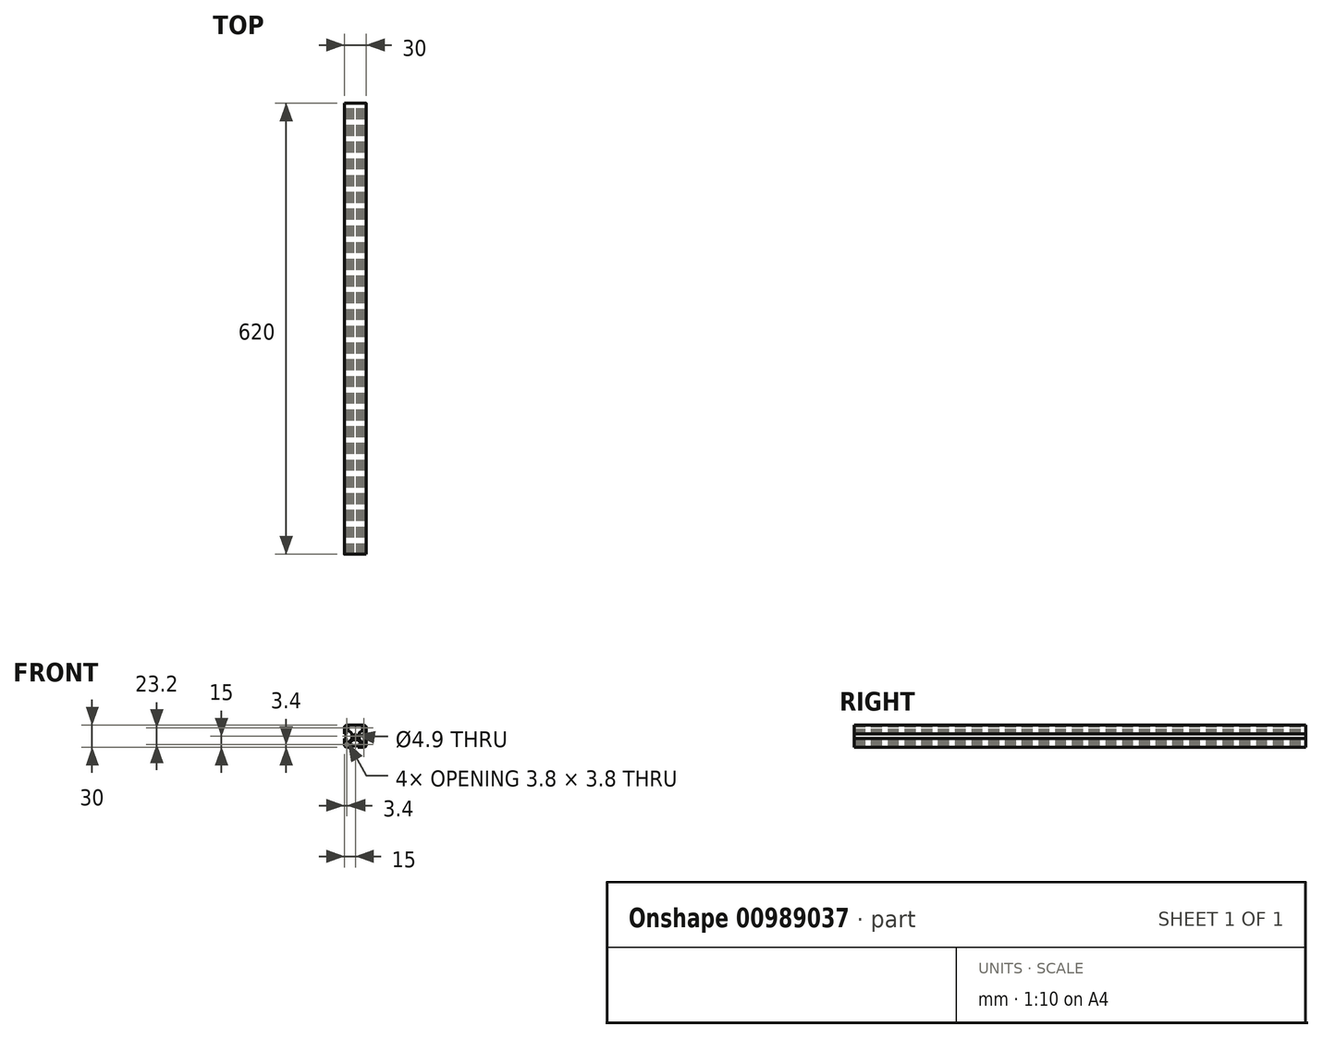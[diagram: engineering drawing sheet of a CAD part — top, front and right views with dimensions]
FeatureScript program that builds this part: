
annotation { "Feature Type Name" : "Feature", "Feature Type Description" : "" }
export const myFeature = defineFeature(function(context is Context, id is Id, definition is map)
    precondition{}
    {
        {
            var Q0;
            Q0=qCreatedBy(makeId("Front.planeOp"),FACE);
            var sketch = newSketch(context, id + "F0", { "sketchPlane" : qUnion([Q0])});
            skLineSegment(sketch, "E0.bottom", {"start": v(-12, 15) * mm, "end": v(12, 15) * mm});
            skLineSegment(sketch, "E0.top", {"start": v(-12, -15) * mm, "end": v(12, -15) * mm});
            skLineSegment(sketch, "E0.left", {"start": v(-15, 12) * mm, "end": v(-15, -12) * mm});
            skLineSegment(sketch, "E0.right", {"start": v(15, 12) * mm, "end": v(15, -12) * mm});
            skPoint(sketch, "E1.visualSharp", {"position": v(-15, 15) * mm});
            skArc(sketch, "E1.filletArc", {"start": v(-12, 15) * mm, "mid": v(-14.12, 14.12) * mm, "end": v(-15, 12) * mm});
            skPoint(sketch, "E2.visualSharp", {"position": v(15, 15) * mm});
            skArc(sketch, "E2.filletArc", {"start": v(15, 12) * mm, "mid": v(14.12, 14.12) * mm, "end": v(12, 15) * mm});
            skPoint(sketch, "E3.visualSharp", {"position": v(15, -15) * mm});
            skArc(sketch, "E3.filletArc", {"start": v(12, -15) * mm, "mid": v(14.12, -14.12) * mm, "end": v(15, -12) * mm});
            skPoint(sketch, "E4.visualSharp", {"position": v(-15, -15) * mm});
            skArc(sketch, "E4.filletArc", {"start": v(-15, -12) * mm, "mid": v(-14.12, -14.12) * mm, "end": v(-12, -15) * mm});
            skCircle(sketch, "E5", {"center": v(0, 0) * mm, "radius": 2.45 * mm});
            skPoint(sketch, "E6", {"position": v(15, 8.22) * mm});
            skPoint(sketch, "E7", {"position": v(15, -8.22) * mm});
            skPoint(sketch, "E8", {"position": v(15, 3.17) * mm});
            skPoint(sketch, "E9", {"position": v(15, -3.18) * mm});
            skLineSegment(sketch, "E10", {"start": v(15, 3.17) * mm, "end": v(13.09, 3.17) * mm});
            skLineSegment(sketch, "E11", {"start": v(13.09, -3.18) * mm, "end": v(15, -3.18) * mm});
            skPoint(sketch, "E12", {"position": v(12.06, -5.83) * mm});
            skPoint(sketch, "E13", {"position": v(12.06, 5.82) * mm});
            skPoint(sketch, "E14", {"position": v(13.5, -5.82) * mm});
            skPoint(sketch, "E15", {"position": v(13.5, 5.82) * mm});
            skPoint(sketch, "E16", {"position": v(13.5, 8.22) * mm});
            skPoint(sketch, "E17", {"position": v(13.5, -8.22) * mm});
            skPoint(sketch, "E18", {"position": v(9.5, 8.22) * mm});
            skPoint(sketch, "E19", {"position": v(9.5, -8.22) * mm});
            skPoint(sketch, "E20", {"position": v(5.1, -3.92) * mm});
            skPoint(sketch, "E21", {"position": v(5.1, 4.08) * mm});
            skLineSegment(sketch, "E22", {"start": v(12.09, -4.16) * mm, "end": v(12.08, -4.81) * mm});
            skLineSegment(sketch, "E23", {"start": v(13.5, -5.82) * mm, "end": v(13.5, -8.22) * mm});
            skLineSegment(sketch, "E24", {"start": v(9.2, -7.94) * mm, "end": v(5.4, -4.21) * mm});
            skLineSegment(sketch, "E25", {"start": v(5.1, 3.65) * mm, "end": v(5.1, -3.5) * mm});
            skLineSegment(sketch, "E26", {"start": v(5.41, 4.38) * mm, "end": v(9.21, 7.95) * mm});
            skLineSegment(sketch, "E27", {"start": v(13.5, 8.22) * mm, "end": v(9.9, 8.22) * mm});
            skLineSegment(sketch, "E28", {"start": v(13.5, 8.22) * mm, "end": v(13.5, 5.82) * mm});
            skLineSegment(sketch, "E29", {"start": v(13.08, 5.82) * mm, "end": v(13.5, 5.82) * mm});
            skLineSegment(sketch, "E30", {"start": v(12.08, 4.81) * mm, "end": v(12.09, 4.16) * mm});
            skLineSegment(sketch, "E31", {"start": v(13.08, -5.83) * mm, "end": v(13.5, -5.83) * mm});
            skLineSegment(sketch, "E32", {"start": v(13.5, -8.22) * mm, "end": v(9.9, -8.22) * mm});
            skLineSegment(sketch, "E33", {"start": v(13.5, -8.22) * mm, "end": v(13.5, -5.82) * mm});
            skArc(sketch, "E34.filletArc", {"start": v(9.9, 8.22) * mm, "mid": v(9.53, 8.15) * mm, "end": v(9.21, 7.95) * mm});
            skArc(sketch, "E35.filletArc", {"start": v(5.41, 4.38) * mm, "mid": v(5.18, 4.04) * mm, "end": v(5.1, 3.65) * mm});
            skArc(sketch, "E36.filletArc", {"start": v(5.1, -3.5) * mm, "mid": v(5.18, -3.89) * mm, "end": v(5.4, -4.21) * mm});
            skArc(sketch, "E37.filletArc", {"start": v(9.2, -7.94) * mm, "mid": v(9.53, -8.15) * mm, "end": v(9.9, -8.22) * mm});
            skArc(sketch, "E38.filletArc", {"start": v(12.08, -4.81) * mm, "mid": v(12.36, -5.53) * mm, "end": v(13.08, -5.83) * mm});
            skPoint(sketch, "E39.visualSharp", {"position": v(12.1, -3.18) * mm});
            skArc(sketch, "E39.filletArc", {"start": v(13.09, -3.18) * mm, "mid": v(12.38, -3.46) * mm, "end": v(12.09, -4.16) * mm});
            skPoint(sketch, "E40.visualSharp", {"position": v(12.1, 3.17) * mm});
            skArc(sketch, "E40.filletArc", {"start": v(12.09, 4.16) * mm, "mid": v(12.38, 3.46) * mm, "end": v(13.09, 3.17) * mm});
            skArc(sketch, "E41.filletArc", {"start": v(13.08, 5.82) * mm, "mid": v(12.36, 5.53) * mm, "end": v(12.08, 4.81) * mm});
            skArc(sketch, "E42.MirrorCS", {"start": v(-5.1, -3.5) * mm, "mid": v(-5.18, -3.89) * mm, "end": v(-5.4, -4.21) * mm});
            skLineSegment(sketch, "E43.MirrorCS", {"start": v(-13.08, -5.83) * mm, "end": v(-13.5, -5.83) * mm});
            skArc(sketch, "E44.MirrorCS", {"start": v(-9.2, -7.94) * mm, "mid": v(-9.53, -8.15) * mm, "end": v(-9.9, -8.22) * mm});
            skLineSegment(sketch, "E45.MirrorCS", {"start": v(-13.08, 5.82) * mm, "end": v(-13.5, 5.82) * mm});
            skArc(sketch, "E46.MirrorCS", {"start": v(-5.41, 4.38) * mm, "mid": v(-5.18, 4.04) * mm, "end": v(-5.1, 3.65) * mm});
            skArc(sketch, "E47.MirrorCS", {"start": v(-9.9, 8.22) * mm, "mid": v(-9.53, 8.15) * mm, "end": v(-9.21, 7.95) * mm});
            skArc(sketch, "E48.MirrorCS", {"start": v(-13.08, 5.82) * mm, "mid": v(-12.36, 5.53) * mm, "end": v(-12.08, 4.81) * mm});
            skLineSegment(sketch, "E49.MirrorCS", {"start": v(-12.08, 4.81) * mm, "end": v(-12.09, 4.16) * mm});
            skLineSegment(sketch, "E50.MirrorCS", {"start": v(-12.09, -4.16) * mm, "end": v(-12.08, -4.81) * mm});
            skArc(sketch, "E51.MirrorCS", {"start": v(-12.08, -4.81) * mm, "mid": v(-12.36, -5.53) * mm, "end": v(-13.08, -5.83) * mm});
            skLineSegment(sketch, "E52.MirrorCS", {"start": v(-13.5, -8.22) * mm, "end": v(-13.5, -5.82) * mm});
            skLineSegment(sketch, "E53.MirrorCS", {"start": v(-13.5, -5.82) * mm, "end": v(-13.5, -8.22) * mm});
            skLineSegment(sketch, "E54.MirrorCS", {"start": v(-13.09, -3.18) * mm, "end": v(-15, -3.18) * mm});
            skArc(sketch, "E55.MirrorCS", {"start": v(-12.09, 4.16) * mm, "mid": v(-12.38, 3.46) * mm, "end": v(-13.09, 3.17) * mm});
            skArc(sketch, "E56.MirrorCS", {"start": v(-13.09, -3.18) * mm, "mid": v(-12.38, -3.46) * mm, "end": v(-12.09, -4.16) * mm});
            skLineSegment(sketch, "E57.MirrorCS", {"start": v(-15, 3.17) * mm, "end": v(-13.09, 3.17) * mm});
            skPoint(sketch, "E58.MirrorP", {"position": v(-5.1, -3.92) * mm});
            skPoint(sketch, "E59.MirrorP", {"position": v(-9.5, -8.22) * mm});
            skPoint(sketch, "E60.MirrorP", {"position": v(-13.5, -8.22) * mm});
            skPoint(sketch, "E61.MirrorP", {"position": v(-12.06, 5.82) * mm});
            skPoint(sketch, "E62.MirrorP", {"position": v(-5.1, 4.08) * mm});
            skLineSegment(sketch, "E63.MirrorCS", {"start": v(-13.5, 8.22) * mm, "end": v(-13.5, 5.82) * mm});
            skPoint(sketch, "E64.MirrorP", {"position": v(-12.06, -5.83) * mm});
            skPoint(sketch, "E65.MirrorP", {"position": v(-9.5, 8.22) * mm});
            skPoint(sketch, "E66.MirrorP", {"position": v(-15, 8.22) * mm});
            skPoint(sketch, "E67.MirrorP", {"position": v(-13.5, 5.82) * mm});
            skLineSegment(sketch, "E68.MirrorCS", {"start": v(-13.5, 8.22) * mm, "end": v(-9.9, 8.22) * mm});
            skPoint(sketch, "E69.MirrorP", {"position": v(-13.5, -5.82) * mm});
            skLineSegment(sketch, "E70.MirrorCS", {"start": v(-13.5, -8.22) * mm, "end": v(-9.9, -8.22) * mm});
            skLineSegment(sketch, "E71.MirrorCS", {"start": v(-5.1, 3.65) * mm, "end": v(-5.1, -3.5) * mm});
            skPoint(sketch, "E72.MirrorP", {"position": v(-13.5, 8.22) * mm});
            skPoint(sketch, "E73.MirrorP", {"position": v(-15, -3.18) * mm});
            skPoint(sketch, "E74.MirrorP", {"position": v(-12.1, 3.17) * mm});
            skPoint(sketch, "E75.MirrorP", {"position": v(-15, -8.22) * mm});
            skPoint(sketch, "E76.MirrorP", {"position": v(-12.1, -3.18) * mm});
            skLineSegment(sketch, "E77.MirrorCS", {"start": v(-5.41, 4.38) * mm, "end": v(-9.21, 7.95) * mm});
            skLineSegment(sketch, "E78.MirrorCS", {"start": v(-9.2, -7.94) * mm, "end": v(-5.4, -4.21) * mm});
            skPoint(sketch, "E79.MirrorP", {"position": v(-15, 3.17) * mm});
            skArc(sketch, "E80.MirrorCS", {"start": v(-3.5, 5.1) * mm, "mid": v(-3.89, 5.18) * mm, "end": v(-4.21, 5.4) * mm});
            skLineSegment(sketch, "E81.MirrorCS", {"start": v(-5.82, 13.08) * mm, "end": v(-5.82, 13.5) * mm});
            skArc(sketch, "E82.MirrorCS", {"start": v(-7.94, 9.2) * mm, "mid": v(-8.15, 9.53) * mm, "end": v(-8.22, 9.9) * mm});
            skLineSegment(sketch, "E83.MirrorCS", {"start": v(5.83, 13.08) * mm, "end": v(5.83, 13.5) * mm});
            skArc(sketch, "E84.MirrorCS", {"start": v(4.38, 5.41) * mm, "mid": v(4.04, 5.18) * mm, "end": v(3.65, 5.1) * mm});
            skArc(sketch, "E85.MirrorCS", {"start": v(8.23, 9.9) * mm, "mid": v(8.15, 9.53) * mm, "end": v(7.95, 9.21) * mm});
            skArc(sketch, "E86.MirrorCS", {"start": v(5.83, 13.08) * mm, "mid": v(5.53, 12.36) * mm, "end": v(4.81, 12.08) * mm});
            skLineSegment(sketch, "E87.MirrorCS", {"start": v(4.81, 12.08) * mm, "end": v(4.16, 12.09) * mm});
            skLineSegment(sketch, "E88.MirrorCS", {"start": v(-4.16, 12.09) * mm, "end": v(-4.81, 12.08) * mm});
            skArc(sketch, "E89.MirrorCS", {"start": v(-4.81, 12.08) * mm, "mid": v(-5.53, 12.36) * mm, "end": v(-5.82, 13.08) * mm});
            skLineSegment(sketch, "E90.MirrorCS", {"start": v(-8.22, 13.5) * mm, "end": v(-5.82, 13.5) * mm});
            skLineSegment(sketch, "E91.MirrorCS", {"start": v(-5.82, 13.5) * mm, "end": v(-8.22, 13.5) * mm});
            skLineSegment(sketch, "E92.MirrorCS", {"start": v(-3.17, 13.09) * mm, "end": v(-3.17, 15) * mm});
            skArc(sketch, "E93.MirrorCS", {"start": v(4.16, 12.09) * mm, "mid": v(3.46, 12.38) * mm, "end": v(3.18, 13.09) * mm});
            skArc(sketch, "E94.MirrorCS", {"start": v(-3.17, 13.09) * mm, "mid": v(-3.46, 12.38) * mm, "end": v(-4.16, 12.09) * mm});
            skLineSegment(sketch, "E95.MirrorCS", {"start": v(3.18, 15) * mm, "end": v(3.18, 13.09) * mm});
            skPoint(sketch, "E96.MirrorP", {"position": v(-3.92, 5.1) * mm});
            skPoint(sketch, "E97.MirrorP", {"position": v(-8.22, 9.5) * mm});
            skPoint(sketch, "E98.MirrorP", {"position": v(-8.22, 13.5) * mm});
            skPoint(sketch, "E99.MirrorP", {"position": v(5.83, 12.06) * mm});
            skPoint(sketch, "E100.MirrorP", {"position": v(4.08, 5.1) * mm});
            skLineSegment(sketch, "E101.MirrorCS", {"start": v(8.23, 13.5) * mm, "end": v(5.83, 13.5) * mm});
            skPoint(sketch, "E102.MirrorP", {"position": v(-5.82, 12.06) * mm});
            skPoint(sketch, "E103.MirrorP", {"position": v(8.23, 9.5) * mm});
            skPoint(sketch, "E104.MirrorP", {"position": v(8.23, 15) * mm});
            skPoint(sketch, "E105.MirrorP", {"position": v(5.83, 13.5) * mm});
            skLineSegment(sketch, "E106.MirrorCS", {"start": v(8.23, 13.5) * mm, "end": v(8.23, 9.9) * mm});
            skPoint(sketch, "E107.MirrorP", {"position": v(-5.82, 13.5) * mm});
            skLineSegment(sketch, "E108.MirrorCS", {"start": v(-8.22, 13.5) * mm, "end": v(-8.22, 9.9) * mm});
            skLineSegment(sketch, "E109.MirrorCS", {"start": v(3.65, 5.1) * mm, "end": v(-3.5, 5.1) * mm});
            skPoint(sketch, "E110.MirrorP", {"position": v(8.23, 13.5) * mm});
            skPoint(sketch, "E111.MirrorP", {"position": v(-3.17, 15) * mm});
            skPoint(sketch, "E112.MirrorP", {"position": v(3.18, 12.1) * mm});
            skPoint(sketch, "E113.MirrorP", {"position": v(-8.22, 15) * mm});
            skPoint(sketch, "E114.MirrorP", {"position": v(-3.17, 12.1) * mm});
            skLineSegment(sketch, "E115.MirrorCS", {"start": v(4.38, 5.41) * mm, "end": v(7.95, 9.21) * mm});
            skLineSegment(sketch, "E116.MirrorCS", {"start": v(-7.94, 9.2) * mm, "end": v(-4.21, 5.4) * mm});
            skPoint(sketch, "E117.MirrorP", {"position": v(3.18, 15) * mm});
            skPoint(sketch, "E118", {"position": v(-8.22, -15) * mm});
            skArc(sketch, "E119.MirrorCS", {"start": v(3.5, -5.1) * mm, "mid": v(3.89, -5.18) * mm, "end": v(4.21, -5.4) * mm});
            skLineSegment(sketch, "E120.MirrorCS", {"start": v(5.83, -13.08) * mm, "end": v(5.83, -13.5) * mm});
            skArc(sketch, "E121.MirrorCS", {"start": v(7.94, -9.2) * mm, "mid": v(8.15, -9.53) * mm, "end": v(8.23, -9.9) * mm});
            skLineSegment(sketch, "E122.MirrorCS", {"start": v(-5.82, -13.08) * mm, "end": v(-5.82, -13.5) * mm});
            skArc(sketch, "E123.MirrorCS", {"start": v(-4.38, -5.41) * mm, "mid": v(-4.04, -5.18) * mm, "end": v(-3.65, -5.1) * mm});
            skArc(sketch, "E124.MirrorCS", {"start": v(-8.22, -9.9) * mm, "mid": v(-8.15, -9.53) * mm, "end": v(-7.95, -9.21) * mm});
            skArc(sketch, "E125.MirrorCS", {"start": v(-5.82, -13.08) * mm, "mid": v(-5.53, -12.36) * mm, "end": v(-4.81, -12.08) * mm});
            skLineSegment(sketch, "E126.MirrorCS", {"start": v(-4.81, -12.08) * mm, "end": v(-4.16, -12.09) * mm});
            skLineSegment(sketch, "E127.MirrorCS", {"start": v(4.16, -12.09) * mm, "end": v(4.81, -12.08) * mm});
            skArc(sketch, "E128.MirrorCS", {"start": v(4.81, -12.08) * mm, "mid": v(5.53, -12.36) * mm, "end": v(5.83, -13.08) * mm});
            skLineSegment(sketch, "E129.MirrorCS", {"start": v(8.23, -13.5) * mm, "end": v(5.83, -13.5) * mm});
            skLineSegment(sketch, "E130.MirrorCS", {"start": v(5.83, -13.5) * mm, "end": v(8.23, -13.5) * mm});
            skLineSegment(sketch, "E131.MirrorCS", {"start": v(3.18, -13.09) * mm, "end": v(3.18, -15) * mm});
            skArc(sketch, "E132.MirrorCS", {"start": v(-4.16, -12.09) * mm, "mid": v(-3.46, -12.38) * mm, "end": v(-3.17, -13.09) * mm});
            skArc(sketch, "E133.MirrorCS", {"start": v(3.18, -13.09) * mm, "mid": v(3.46, -12.38) * mm, "end": v(4.16, -12.09) * mm});
            skLineSegment(sketch, "E134.MirrorCS", {"start": v(-3.17, -15) * mm, "end": v(-3.17, -13.09) * mm});
            skPoint(sketch, "E135.MirrorP", {"position": v(3.92, -5.1) * mm});
            skPoint(sketch, "E136.MirrorP", {"position": v(8.23, -9.5) * mm});
            skPoint(sketch, "E137.MirrorP", {"position": v(8.23, -13.5) * mm});
            skPoint(sketch, "E138.MirrorP", {"position": v(-5.82, -12.06) * mm});
            skPoint(sketch, "E139.MirrorP", {"position": v(-4.08, -5.1) * mm});
            skLineSegment(sketch, "E140.MirrorCS", {"start": v(-8.22, -13.5) * mm, "end": v(-5.82, -13.5) * mm});
            skPoint(sketch, "E141.MirrorP", {"position": v(5.83, -12.06) * mm});
            skPoint(sketch, "E142.MirrorP", {"position": v(-8.22, -9.5) * mm});
            skPoint(sketch, "E143.MirrorP", {"position": v(-5.82, -13.5) * mm});
            skLineSegment(sketch, "E144.MirrorCS", {"start": v(-8.22, -13.5) * mm, "end": v(-8.22, -9.9) * mm});
            skPoint(sketch, "E145.MirrorP", {"position": v(5.83, -13.5) * mm});
            skLineSegment(sketch, "E146.MirrorCS", {"start": v(8.23, -13.5) * mm, "end": v(8.23, -9.9) * mm});
            skLineSegment(sketch, "E147.MirrorCS", {"start": v(-3.65, -5.1) * mm, "end": v(3.5, -5.1) * mm});
            skPoint(sketch, "E148.MirrorP", {"position": v(-8.22, -13.5) * mm});
            skPoint(sketch, "E149.MirrorP", {"position": v(3.18, -15) * mm});
            skPoint(sketch, "E150.MirrorP", {"position": v(-3.17, -12.1) * mm});
            skPoint(sketch, "E151.MirrorP", {"position": v(8.23, -15) * mm});
            skPoint(sketch, "E152.MirrorP", {"position": v(3.18, -12.1) * mm});
            skLineSegment(sketch, "E153.MirrorCS", {"start": v(-4.38, -5.41) * mm, "end": v(-7.95, -9.21) * mm});
            skLineSegment(sketch, "E154.MirrorCS", {"start": v(7.94, -9.2) * mm, "end": v(4.21, -5.4) * mm});
            skPoint(sketch, "E155.MirrorP", {"position": v(-3.17, -15) * mm});
            skLineSegment(sketch, "E156.bottom", {"start": v(-13.5, -9.7) * mm, "end": v(-9.7, -9.7) * mm});
            skLineSegment(sketch, "E156.top", {"start": v(-11.5, -13.5) * mm, "end": v(-9.7, -13.5) * mm});
            skLineSegment(sketch, "E156.left", {"start": v(-13.5, -9.7) * mm, "end": v(-13.5, -11.5) * mm});
            skLineSegment(sketch, "E156.right", {"start": v(-9.7, -9.7) * mm, "end": v(-9.7, -13.5) * mm});
            skPoint(sketch, "E157.visualSharp", {"position": v(-13.5, -13.5) * mm});
            skArc(sketch, "E157.filletArc", {"start": v(-13.5, -11.5) * mm, "mid": v(-12.91, -12.91) * mm, "end": v(-11.5, -13.5) * mm});
            skPoint(sketch, "E158", {"position": v(-11.6, -11.6) * mm});
            skPoint(sketch, "E159.MirrorP", {"position": v(-11.6, 11.6) * mm});
            skLineSegment(sketch, "E160.MirrorCS", {"start": v(-11.5, 13.5) * mm, "end": v(-9.7, 13.5) * mm});
            skLineSegment(sketch, "E161.MirrorCS", {"start": v(-9.7, 9.7) * mm, "end": v(-9.7, 13.5) * mm});
            skLineSegment(sketch, "E162.MirrorCS", {"start": v(-13.5, 9.7) * mm, "end": v(-9.7, 9.7) * mm});
            skLineSegment(sketch, "E163.MirrorCS", {"start": v(-13.5, 9.7) * mm, "end": v(-13.5, 11.5) * mm});
            skPoint(sketch, "E164.MirrorP", {"position": v(-13.5, 13.5) * mm});
            skArc(sketch, "E165.MirrorCS", {"start": v(-13.5, 11.5) * mm, "mid": v(-12.91, 12.91) * mm, "end": v(-11.5, 13.5) * mm});
            skPoint(sketch, "E166.MirrorP", {"position": v(11.6, 11.6) * mm});
            skLineSegment(sketch, "E167.MirrorCS", {"start": v(11.5, 13.5) * mm, "end": v(9.7, 13.5) * mm});
            skLineSegment(sketch, "E168.MirrorCS", {"start": v(13.5, 9.7) * mm, "end": v(9.7, 9.7) * mm});
            skLineSegment(sketch, "E169.MirrorCS", {"start": v(9.7, 9.7) * mm, "end": v(9.7, 13.5) * mm});
            skLineSegment(sketch, "E170.MirrorCS", {"start": v(13.5, 9.7) * mm, "end": v(13.5, 11.5) * mm});
            skArc(sketch, "E171.MirrorCS", {"start": v(13.5, 11.5) * mm, "mid": v(12.91, 12.91) * mm, "end": v(11.5, 13.5) * mm});
            skPoint(sketch, "E172.MirrorP", {"position": v(11.6, -11.6) * mm});
            skLineSegment(sketch, "E173.MirrorCS", {"start": v(13.5, -9.7) * mm, "end": v(13.5, -11.5) * mm});
            skArc(sketch, "E174.MirrorCS", {"start": v(13.5, -11.5) * mm, "mid": v(12.91, -12.91) * mm, "end": v(11.5, -13.5) * mm});
            skLineSegment(sketch, "E175.MirrorCS", {"start": v(13.5, -9.7) * mm, "end": v(9.7, -9.7) * mm});
            skLineSegment(sketch, "E176.MirrorCS", {"start": v(9.7, -9.7) * mm, "end": v(9.7, -13.5) * mm});
            skLineSegment(sketch, "E177.MirrorCS", {"start": v(11.5, -13.5) * mm, "end": v(9.7, -13.5) * mm});
            skSolve(sketch);
        }
        {
            var Q0;
            {var subQ13=sQuery(id+"F0.wireOp",EDGE,"E1.filletArc");Q0=makeQuery(id+"F0.imprint","IMPRINT",FACE,{"disambiguationData":[TD([[makeQuery(id+"F0.imprint","IMPRINT",EDGE,{"derivedFrom":subQ13}),1.0]])]});}
            extrude(context, id + "F1", {"entities" : qUnion([Q0]), "depth" : 460 * mm, "offsetDistance" : 25 * mm});
        }
        {
            var Q0;
            Q0=makeQuery(id+"F1.opExtrude","CAP_FACE",FACE,{"disambiguationData":[OSD([sQuery(id+"F0.wireOp",EDGE,"E0.bottom"),sQuery(id+"F0.wireOp",EDGE,"E0.top"),sQuery(id+"F0.wireOp",EDGE,"E0.left"),sQuery(id+"F0.wireOp",EDGE,"E0.right"),sQuery(id+"F0.wireOp",EDGE,"E1.filletArc"),sQuery(id+"F0.wireOp",EDGE,"E2.filletArc"),sQuery(id+"F0.wireOp",EDGE,"E3.filletArc"),sQuery(id+"F0.wireOp",EDGE,"E4.filletArc"),sQuery(id+"F0.wireOp",EDGE,"E5"),sQuery(id+"F0.wireOp",EDGE,"E10"),sQuery(id+"F0.wireOp",EDGE,"E11"),sQuery(id+"F0.wireOp",EDGE,"E22"),sQuery(id+"F0.wireOp",EDGE,"E24"),sQuery(id+"F0.wireOp",EDGE,"E25"),sQuery(id+"F0.wireOp",EDGE,"E26"),sQuery(id+"F0.wireOp",EDGE,"E27"),sQuery(id+"F0.wireOp",EDGE,"E28"),sQuery(id+"F0.wireOp",EDGE,"E29"),sQuery(id+"F0.wireOp",EDGE,"E30"),sQuery(id+"F0.wireOp",EDGE,"E31"),sQuery(id+"F0.wireOp",EDGE,"E32"),sQuery(id+"F0.wireOp",EDGE,"E33"),sQuery(id+"F0.wireOp",EDGE,"E34.filletArc"),sQuery(id+"F0.wireOp",EDGE,"E35.filletArc"),sQuery(id+"F0.wireOp",EDGE,"E36.filletArc"),sQuery(id+"F0.wireOp",EDGE,"E37.filletArc"),sQuery(id+"F0.wireOp",EDGE,"E38.filletArc"),sQuery(id+"F0.wireOp",EDGE,"E39.filletArc"),sQuery(id+"F0.wireOp",EDGE,"E40.filletArc"),sQuery(id+"F0.wireOp",EDGE,"E41.filletArc"),sQuery(id+"F0.wireOp",EDGE,"E42.MirrorCS"),sQuery(id+"F0.wireOp",EDGE,"E43.MirrorCS"),sQuery(id+"F0.wireOp",EDGE,"E44.MirrorCS"),sQuery(id+"F0.wireOp",EDGE,"E45.MirrorCS"),sQuery(id+"F0.wireOp",EDGE,"E46.MirrorCS"),sQuery(id+"F0.wireOp",EDGE,"E47.MirrorCS"),sQuery(id+"F0.wireOp",EDGE,"E48.MirrorCS"),sQuery(id+"F0.wireOp",EDGE,"E49.MirrorCS"),sQuery(id+"F0.wireOp",EDGE,"E50.MirrorCS"),sQuery(id+"F0.wireOp",EDGE,"E51.MirrorCS"),sQuery(id+"F0.wireOp",EDGE,"E53.MirrorCS"),sQuery(id+"F0.wireOp",EDGE,"E54.MirrorCS"),sQuery(id+"F0.wireOp",EDGE,"E55.MirrorCS"),sQuery(id+"F0.wireOp",EDGE,"E56.MirrorCS"),sQuery(id+"F0.wireOp",EDGE,"E57.MirrorCS"),sQuery(id+"F0.wireOp",EDGE,"E63.MirrorCS"),sQuery(id+"F0.wireOp",EDGE,"E68.MirrorCS"),sQuery(id+"F0.wireOp",EDGE,"E70.MirrorCS"),sQuery(id+"F0.wireOp",EDGE,"E71.MirrorCS"),sQuery(id+"F0.wireOp",EDGE,"E77.MirrorCS"),sQuery(id+"F0.wireOp",EDGE,"E78.MirrorCS"),sQuery(id+"F0.wireOp",EDGE,"E80.MirrorCS"),sQuery(id+"F0.wireOp",EDGE,"E81.MirrorCS"),sQuery(id+"F0.wireOp",EDGE,"E82.MirrorCS"),sQuery(id+"F0.wireOp",EDGE,"E83.MirrorCS"),sQuery(id+"F0.wireOp",EDGE,"E84.MirrorCS"),sQuery(id+"F0.wireOp",EDGE,"E85.MirrorCS"),sQuery(id+"F0.wireOp",EDGE,"E86.MirrorCS"),sQuery(id+"F0.wireOp",EDGE,"E87.MirrorCS"),sQuery(id+"F0.wireOp",EDGE,"E88.MirrorCS"),sQuery(id+"F0.wireOp",EDGE,"E89.MirrorCS"),sQuery(id+"F0.wireOp",EDGE,"E91.MirrorCS"),sQuery(id+"F0.wireOp",EDGE,"E92.MirrorCS"),sQuery(id+"F0.wireOp",EDGE,"E93.MirrorCS"),sQuery(id+"F0.wireOp",EDGE,"E94.MirrorCS"),sQuery(id+"F0.wireOp",EDGE,"E95.MirrorCS"),sQuery(id+"F0.wireOp",EDGE,"E101.MirrorCS"),sQuery(id+"F0.wireOp",EDGE,"E106.MirrorCS"),sQuery(id+"F0.wireOp",EDGE,"E108.MirrorCS"),sQuery(id+"F0.wireOp",EDGE,"E109.MirrorCS"),sQuery(id+"F0.wireOp",EDGE,"E115.MirrorCS"),sQuery(id+"F0.wireOp",EDGE,"E116.MirrorCS"),sQuery(id+"F0.wireOp",EDGE,"E119.MirrorCS"),sQuery(id+"F0.wireOp",EDGE,"E120.MirrorCS"),sQuery(id+"F0.wireOp",EDGE,"E121.MirrorCS"),sQuery(id+"F0.wireOp",EDGE,"E122.MirrorCS"),sQuery(id+"F0.wireOp",EDGE,"E123.MirrorCS"),sQuery(id+"F0.wireOp",EDGE,"E124.MirrorCS"),sQuery(id+"F0.wireOp",EDGE,"E125.MirrorCS"),sQuery(id+"F0.wireOp",EDGE,"E126.MirrorCS"),sQuery(id+"F0.wireOp",EDGE,"E127.MirrorCS"),sQuery(id+"F0.wireOp",EDGE,"E128.MirrorCS"),sQuery(id+"F0.wireOp",EDGE,"E130.MirrorCS"),sQuery(id+"F0.wireOp",EDGE,"E131.MirrorCS"),sQuery(id+"F0.wireOp",EDGE,"E132.MirrorCS"),sQuery(id+"F0.wireOp",EDGE,"E133.MirrorCS"),sQuery(id+"F0.wireOp",EDGE,"E134.MirrorCS"),sQuery(id+"F0.wireOp",EDGE,"E140.MirrorCS"),sQuery(id+"F0.wireOp",EDGE,"E144.MirrorCS"),sQuery(id+"F0.wireOp",EDGE,"E146.MirrorCS"),sQuery(id+"F0.wireOp",EDGE,"E147.MirrorCS"),sQuery(id+"F0.wireOp",EDGE,"E153.MirrorCS"),sQuery(id+"F0.wireOp",EDGE,"E154.MirrorCS"),sQuery(id+"F0.wireOp",EDGE,"E160.MirrorCS"),sQuery(id+"F0.wireOp",EDGE,"E161.MirrorCS"),sQuery(id+"F0.wireOp",EDGE,"E162.MirrorCS"),sQuery(id+"F0.wireOp",EDGE,"E163.MirrorCS"),sQuery(id+"F0.wireOp",EDGE,"E165.MirrorCS"),sQuery(id+"F0.wireOp",EDGE,"E156.top"),sQuery(id+"F0.wireOp",EDGE,"E156.bottom"),sQuery(id+"F0.wireOp",EDGE,"E156.right"),sQuery(id+"F0.wireOp",EDGE,"E156.left"),sQuery(id+"F0.wireOp",EDGE,"E157.filletArc"),sQuery(id+"F0.wireOp",EDGE,"E167.MirrorCS"),sQuery(id+"F0.wireOp",EDGE,"E168.MirrorCS"),sQuery(id+"F0.wireOp",EDGE,"E169.MirrorCS"),sQuery(id+"F0.wireOp",EDGE,"E170.MirrorCS"),sQuery(id+"F0.wireOp",EDGE,"E171.MirrorCS"),sQuery(id+"F0.wireOp",EDGE,"E173.MirrorCS"),sQuery(id+"F0.wireOp",EDGE,"E174.MirrorCS"),sQuery(id+"F0.wireOp",EDGE,"E175.MirrorCS"),sQuery(id+"F0.wireOp",EDGE,"E176.MirrorCS"),sQuery(id+"F0.wireOp",EDGE,"E177.MirrorCS")])],"isStart":false});
            extrude(context, id + "F2", {"entities" : qUnion([Q0]), "operationType" : NewBodyOperationType.ADD, "depth" : 160 * mm, "offsetDistance" : 25 * mm});
        }
    });
